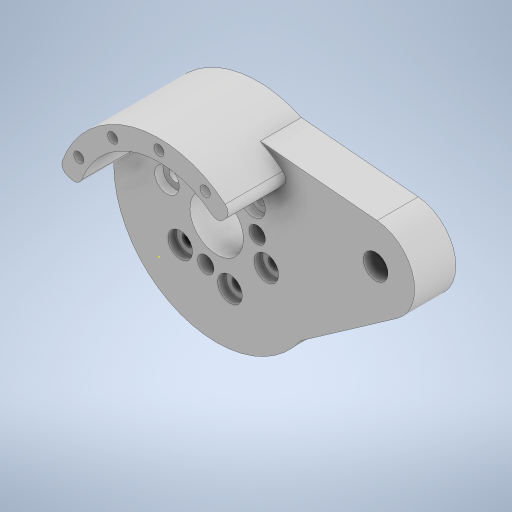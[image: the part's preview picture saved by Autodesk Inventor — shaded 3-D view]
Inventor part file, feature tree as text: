
AUTODESK INVENTOR PART (.ipt)
format: ipt  version: 2024.3 (Build 283343000, 343)  size: 419,328 bytes
history: native  units: mm
features: sketch x9, extrude x5, hole x3, fillet x2, other x1
ambient origin geometry x8: Origin, YZ Plane, XZ Plane, XY Plane, X Axis, Y Axis, Z Axis, Center Point
bodies: Body1 (feature_tree)
feature tree (20):
  other  "ソリッド1"
  extrude  "押し出し1"  Depth=50.0mm
  extrude  "押し出し2"  Depth=14.0mm TaperAngle=0.0deg
  hole  "穴1"  [1 undecoded]
  hole  "穴2"  [1 undecoded]
  sketch  "スケッチ6"
  extrude  "押し出し3"  Depth=50.0mm
  hole  "穴4"  [1 undecoded]
  extrude  "押し出し5"  TaperAngle=0.0deg  [1 undecoded]
  extrude  "押し出し6"  Depth=10.0mm TaperAngle=0.0deg
  fillet  "フィレット3"  Radius=33.0mm
  fillet  "フィレット4"  Radius=25.0mm
  sketch  "スケッチ1"
  sketch  "スケッチ2"
  sketch  "スケッチ3"
  sketch  "スケッチ4"
  sketch  "スケッチ7"
  sketch  "スケッチ9"
  sketch  "スケッチ10"
  sketch  "スケッチ11"
note: 4 required parameter values undecoded (feature->parameter linkage not recoverable at this tier; creation-order binding heuristic only, values carry confidence <= 0.55)
